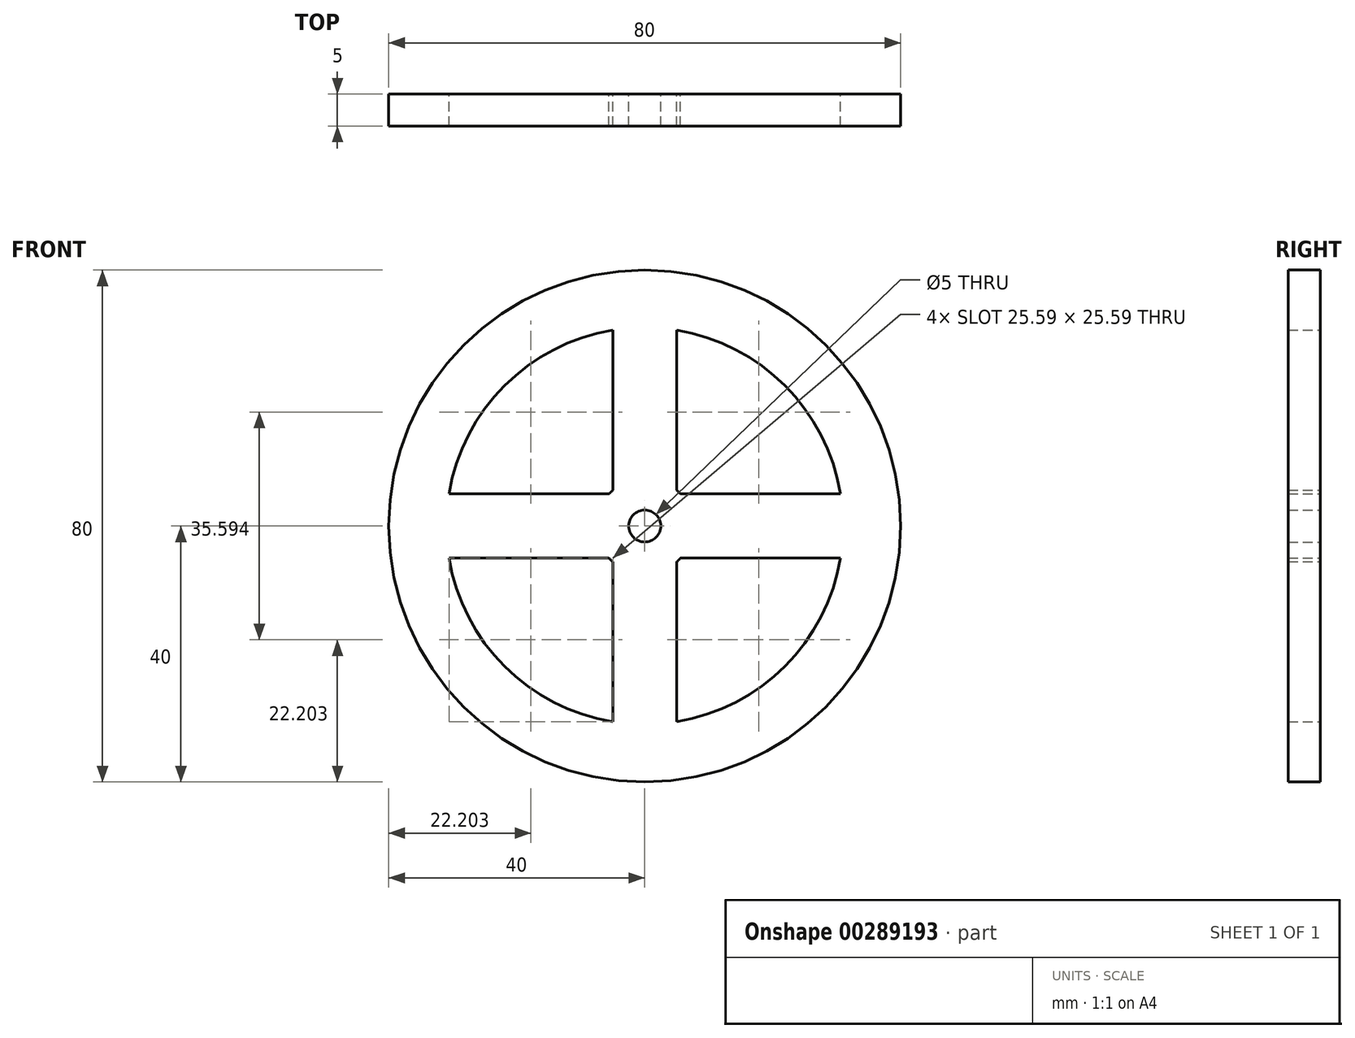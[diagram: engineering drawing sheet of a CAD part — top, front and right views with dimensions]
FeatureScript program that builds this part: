
annotation { "Feature Type Name" : "Feature", "Feature Type Description" : "" }
export const myFeature = defineFeature(function(context is Context, id is Id, definition is map)
    precondition{}
    {
        {
            var Q0;
            Q0=qCreatedBy(makeId("Front.planeOp"),FACE);
            var sketch = newSketch(context, id + "F0", { "sketchPlane" : qUnion([Q0])});
            skArc(sketch, "E0", {"start": v(-5.6, -5) * mm, "mid": v(-5.3, -5.3) * mm, "end": v(-5, -5.6) * mm});
            skCircle(sketch, "E1", {"center": v(0, 0) * mm, "radius": 40 * mm});
            skArc(sketch, "E2", {"start": v(-30.6, -5) * mm, "mid": v(-21.92, -21.92) * mm, "end": v(-5, -30.6) * mm});
            skCircle(sketch, "E3", {"center": v(0, 0) * mm, "radius": 2.5 * mm});
            skLineSegment(sketch, "E4", {"start": v(0, 0) * mm, "end": v(0, 2.5) * mm});
            skLineSegment(sketch, "E5", {"start": v(0, 0) * mm, "end": v(0, -2.5) * mm});
            skLineSegment(sketch, "E6", {"start": v(0, 0) * mm, "end": v(-2.5, 0) * mm});
            skLineSegment(sketch, "E7", {"start": v(7.5, 0) * mm, "end": v(31, 0) * mm, "construction": true});
            skLineSegment(sketch, "E8.0", {"start": v(5, 5.6) * mm, "end": v(5, 30.6) * mm});
            skLineSegment(sketch, "E9.0", {"start": v(-5, 5.6) * mm, "end": v(-5, 30.6) * mm});
            skLineSegment(sketch, "E10.0", {"start": v(-5.6, 5) * mm, "end": v(-30.6, 5) * mm});
            skLineSegment(sketch, "E11.0", {"start": v(-5.6, -5) * mm, "end": v(-30.6, -5) * mm});
            skLineSegment(sketch, "E12.0", {"start": v(-5, -5.6) * mm, "end": v(-5, -30.6) * mm});
            skLineSegment(sketch, "E13.0", {"start": v(5, -5.6) * mm, "end": v(5, -30.6) * mm});
            skLineSegment(sketch, "E14.0", {"start": v(5.6, -5) * mm, "end": v(30.6, -5) * mm});
            skLineSegment(sketch, "E15.0", {"start": v(5.6, 5) * mm, "end": v(30.6, 5) * mm});
            skLineSegment(sketch, "E16", {"start": v(2.5, 0) * mm, "end": v(0, 0) * mm});
            skArc(sketch, "E17.trimOffspring", {"start": v(5, -30.6) * mm, "mid": v(21.92, -21.92) * mm, "end": v(30.6, -5) * mm});
            skArc(sketch, "E18.trimOffspring", {"start": v(30.6, 5) * mm, "mid": v(21.92, 21.92) * mm, "end": v(5, 30.6) * mm});
            skArc(sketch, "E19.trimOffspring", {"start": v(-5, 30.6) * mm, "mid": v(-21.92, 21.92) * mm, "end": v(-30.6, 5) * mm});
            skLineSegment(sketch, "E20.trimOffspring", {"start": v(0, 7.5) * mm, "end": v(0, 31) * mm, "construction": true});
            skLineSegment(sketch, "E21.trimOffspring", {"start": v(0, -7.5) * mm, "end": v(0, -31) * mm, "construction": true});
            skLineSegment(sketch, "E22.trimOffspring", {"start": v(-7.5, 0) * mm, "end": v(-31, 0) * mm, "construction": true});
            skArc(sketch, "E23.trimOffspring", {"start": v(5, -5.6) * mm, "mid": v(5.3, -5.3) * mm, "end": v(5.6, -5) * mm});
            skArc(sketch, "E24.trimOffspring", {"start": v(-5, 5.6) * mm, "mid": v(-5.3, 5.3) * mm, "end": v(-5.6, 5) * mm});
            skArc(sketch, "E25.trimOffspring", {"start": v(5.6, 5) * mm, "mid": v(5.3, 5.3) * mm, "end": v(5, 5.6) * mm});
            skLineSegment(sketch, "E26", {"start": v(7.5, 0) * mm, "end": v(2.5, 0) * mm});
            skLineSegment(sketch, "E27", {"start": v(0, 7.5) * mm, "end": v(0, -7.5) * mm, "construction": true});
            skLineSegment(sketch, "E28", {"start": v(-7.5, 0) * mm, "end": v(7.5, 0) * mm, "construction": true});
            skSolve(sketch);
        }
        {
            var Q0;
            Q0 = qSketchRegion(id + "F0", true);
            extrude(context, id + "F1", {"entities" : qUnion([Q0]), "endBound" : BoundingType.SYMMETRIC, "depth" : 5 * mm});
        }
    });
